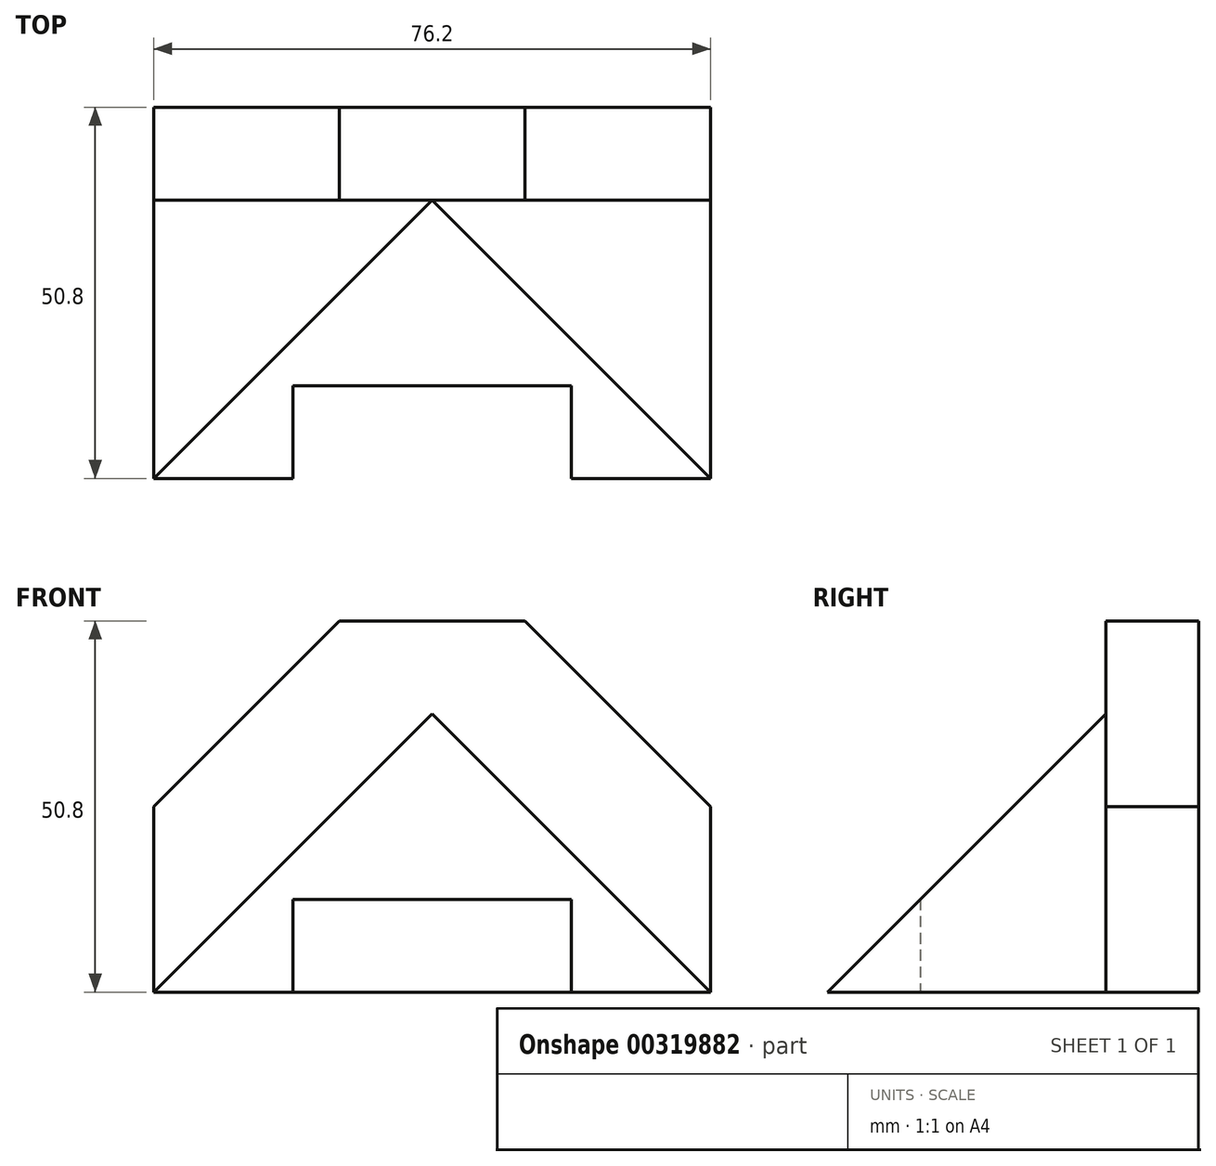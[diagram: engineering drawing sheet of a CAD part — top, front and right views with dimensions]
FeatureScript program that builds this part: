
annotation { "Feature Type Name" : "Feature", "Feature Type Description" : "" }
export const myFeature = defineFeature(function(context is Context, id is Id, definition is map)
    precondition{}
    {
        {
            var Q0;
            Q0=qCreatedBy(makeId("Top.planeOp"),FACE);
            var sketch = newSketch(context, id + "F0", { "sketchPlane" : qUnion([Q0])});
            skLineSegment(sketch, "E0.bottom", {"start": v(0, 0) * mm, "end": v(76.2, 0) * mm});
            skLineSegment(sketch, "E0.top", {"start": v(0, 50.8) * mm, "end": v(76.2, 50.8) * mm});
            skLineSegment(sketch, "E0.left", {"start": v(0, 0) * mm, "end": v(0, 50.8) * mm});
            skLineSegment(sketch, "E0.right", {"start": v(76.2, 0) * mm, "end": v(76.2, 50.8) * mm});
            skSolve(sketch);
        }
        {
            var Q0;
            Q0 = qSketchRegion(id + "F0", true);
            extrude(context, id + "F1", {"entities" : qUnion([Q0]), "depth" : 50.8 * mm});
        }
        {
            var Q0;
            Q0=makeQuery(id+"F1.opExtrude","SWEPT_FACE",FACE,{"disambiguationData":[OSD([sQuery(id+"F0.wireOp",EDGE,"E0.bottom")])]});
            var sketch = newSketch(context, id + "F2", { "sketchPlane" : qUnion([Q0])});
            skLineSegment(sketch, "E1", {"start": v(0, 38.1) * mm, "end": v(76.2, 38.1) * mm, "construction": true});
            skLineSegment(sketch, "E2", {"start": v(0, 0) * mm, "end": v(38.1, 38.1) * mm});
            skLineSegment(sketch, "E3", {"start": v(38.1, 38.1) * mm, "end": v(76.2, 0) * mm});
            skLineSegment(sketch, "E4", {"start": v(19.05, 0) * mm, "end": v(19.05, 12.7) * mm});
            skLineSegment(sketch, "E5", {"start": v(19.05, 12.7) * mm, "end": v(57.15, 12.7) * mm});
            skLineSegment(sketch, "E6", {"start": v(57.15, 12.7) * mm, "end": v(57.15, 0) * mm});
            skSolve(sketch);
        }
        {
            var Q0;
            Q0=makeQuery(id+"F2.imprint","IMPRINT",FACE,{"disambiguationData":[TD([[makeQuery(id+"F2.imprint","IMPRINT",EDGE,{"derivedFrom":sQuery(id+"F2.wireOp",EDGE,"E2")}),1.0]])]});
            extrude(context, id + "F3", {"entities" : qUnion([Q0]), "operationType" : NewBodyOperationType.REMOVE, "oppositeDirection" : true, "depth" : 38.1 * mm});
        }
        {
            var Q0;
            Q0=makeQuery(id+"F3.boolean.opBoolean","COPY",FACE,{"derivedFrom":makeQuery(id+"F3.opExtrude","SWEPT_FACE",FACE,{"disambiguationData":[OSD([sQuery(id+"F2.wireOp",EDGE,"E3")])]})});
            var sketch = newSketch(context, id + "F4", { "sketchPlane" : qUnion([Q0])});
            skLineSegment(sketch, "E7", {"start": v(0, -53.88) * mm, "end": v(38.1, 0) * mm});
            skSolve(sketch);
        }
        {
            var Q0;
            Q0=makeQuery(id+"F3.boolean.opBoolean","COPY",FACE,{"derivedFrom":makeQuery(id+"F3.opExtrude","CAP_FACE",FACE,{"disambiguationData":[OSD([sQuery(id+"F0.wireOp",EDGE,"E0.bottom"),sQuery(id+"F0.wireOp",EDGE,"E0.left"),sQuery(id+"F0.wireOp",EDGE,"E0.right"),sQuery(id+"F2.wireOp",EDGE,"E2"),sQuery(id+"F2.wireOp",EDGE,"E3")])],"isStart":false})});
            var sketch = newSketch(context, id + "F5", { "sketchPlane" : qUnion([Q0])});
            skPoint(sketch, "E8.0", {"position": v(25.4, 50.8) * mm});
            skPoint(sketch, "E9.0", {"position": v(50.8, 50.8) * mm});
            skLineSegment(sketch, "E10", {"start": v(0, 0) * mm, "end": v(0, 25.4) * mm});
            skLineSegment(sketch, "E11", {"start": v(76.2, 0) * mm, "end": v(76.2, 25.4) * mm});
            skLineSegment(sketch, "E12", {"start": v(25.4, 50.8) * mm, "end": v(0, 25.4) * mm});
            skLineSegment(sketch, "E13", {"start": v(50.8, 50.8) * mm, "end": v(76.2, 25.4) * mm});
            skSolve(sketch);
        }
        {
            var Q0;
            Q0 = qSketchRegion(id + "F5", true);
            var Q1;
            {var subQ0=sQuery(id+"F5.wireOp",EDGE,"E12");Q1=makeQuery(id+"F5.imprint","IMPRINT",FACE,{"disambiguationData":[TD([[makeQuery(id+"F5.imprint","IMPRINT",EDGE,{"derivedFrom":subQ0}),-1.0]])]});}
            var Q2;
            {var subQ0=sQuery(id+"F5.wireOp",EDGE,"E13");Q2=makeQuery(id+"F5.imprint","IMPRINT",FACE,{"disambiguationData":[TD([[makeQuery(id+"F5.imprint","IMPRINT",EDGE,{"derivedFrom":subQ0}),1.0]])]});}
            extrude(context, id + "F6", {"entities" : qUnion([Q0, Q1, Q2]), "operationType" : NewBodyOperationType.REMOVE, "oppositeDirection" : true, "depth" : 25.4 * mm});
        }
        {
            var Q0;
            Q0=qCreatedBy(makeId("Right.planeOp"),FACE);
            var sketch = newSketch(context, id + "F7", { "sketchPlane" : qUnion([Q0])});
            skLineSegment(sketch, "E14.0", {"start": v(38.1, 38.1) * mm, "end": v(0, 38.1) * mm});
            skLineSegment(sketch, "E15.0", {"start": v(0, 0) * mm, "end": v(0, 38.1) * mm});
            skLineSegment(sketch, "E16", {"start": v(38.1, 38.1) * mm, "end": v(0, 0) * mm});
            skSolve(sketch);
        }
        {
            var Q0;
            Q0 = qSketchRegion(id + "F7", true);
            extrude(context, id + "F8", {"entities" : qUnion([Q0]), "operationType" : NewBodyOperationType.REMOVE, "endBound" : BoundingType.THROUGH_ALL, "depth" : 25.4 * mm});
        }
        {
            var Q0;
            Q0=makeQuery(id+"F1.opExtrude","CAP_FACE",FACE,{"disambiguationData":[OSD([sQuery(id+"F0.wireOp",EDGE,"E0.bottom"),sQuery(id+"F0.wireOp",EDGE,"E0.top"),sQuery(id+"F0.wireOp",EDGE,"E0.left"),sQuery(id+"F0.wireOp",EDGE,"E0.right")])],"isStart":true});
            var sketch = newSketch(context, id + "F9", { "sketchPlane" : qUnion([Q0])});
            skLineSegment(sketch, "E17.bottom", {"start": v(19.05, 0) * mm, "end": v(57.15, 0) * mm});
            skLineSegment(sketch, "E17.top", {"start": v(19.05, -12.7) * mm, "end": v(57.15, -12.7) * mm});
            skLineSegment(sketch, "E17.left", {"start": v(19.05, 0) * mm, "end": v(19.05, -12.7) * mm});
            skLineSegment(sketch, "E17.right", {"start": v(57.15, 0) * mm, "end": v(57.15, -12.7) * mm});
            skSolve(sketch);
        }
        {
            var Q0;
            Q0=makeQuery(id+"F9.imprint","IMPRINT",FACE,{"disambiguationData":[TD([[makeQuery(id+"F9.imprint","IMPRINT",EDGE,{"derivedFrom":sQuery(id+"F9.wireOp",EDGE,"E17.bottom")}),-1.0]])]});
            extrude(context, id + "F10", {"entities" : qUnion([Q0]), "operationType" : NewBodyOperationType.REMOVE, "oppositeDirection" : true, "depth" : 25.4 * mm});
        }
    });
